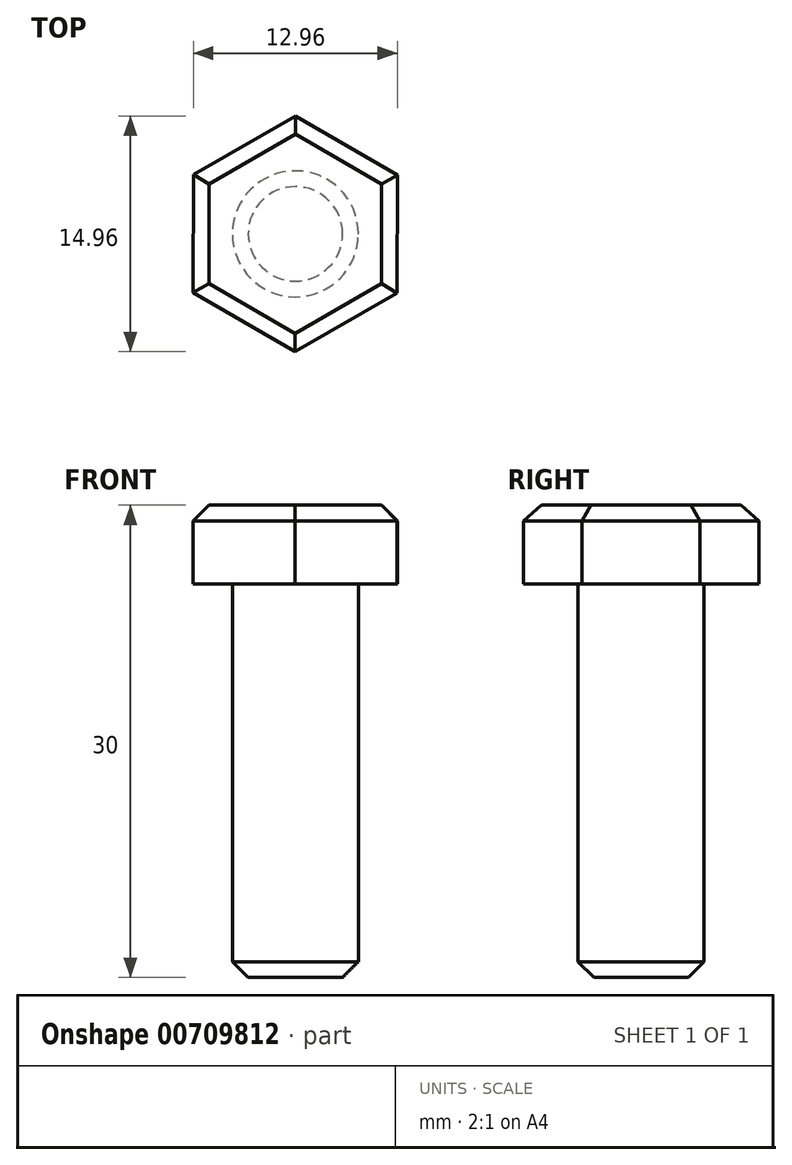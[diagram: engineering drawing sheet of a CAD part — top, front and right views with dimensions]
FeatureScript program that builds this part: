
annotation { "Feature Type Name" : "Feature", "Feature Type Description" : "" }
export const myFeature = defineFeature(function(context is Context, id is Id, definition is map)
    precondition{}
    {
        {
            var Q0;
            Q0=qCreatedBy(makeId("Top.planeOp"),FACE);
            var sketch = newSketch(context, id + "F0", { "sketchPlane" : qUnion([Q0])});
            skCircle(sketch, "E0.cCircle", {"center": v(0, 0) * mm, "radius": 6.48 * mm, "construction": true});
            skLineSegment(sketch, "E0.0", {"start": v(6.47, -3.75) * mm, "end": v(-0.01, -7.48) * mm});
            skLineSegment(sketch, "E0.1", {"start": v(-0.01, -7.48) * mm, "end": v(-6.48, -3.73) * mm});
            skLineSegment(sketch, "E0.2", {"start": v(-6.48, -3.73) * mm, "end": v(-6.47, 3.75) * mm});
            skLineSegment(sketch, "E0.3", {"start": v(-6.47, 3.75) * mm, "end": v(0.01, 7.48) * mm});
            skLineSegment(sketch, "E0.4", {"start": v(0.01, 7.48) * mm, "end": v(6.48, 3.73) * mm});
            skLineSegment(sketch, "E0.5", {"start": v(6.48, 3.73) * mm, "end": v(6.47, -3.75) * mm});
            skPoint(sketch, "E0.0.midPoint", {"position": v(3.23, -5.61) * mm});
            skSolve(sketch);
        }
        {
            var Q0;
            Q0 = qSketchRegion(id + "F0", true);
            extrude(context, id + "F1", {"entities" : qUnion([Q0]), "depth" : 5 * mm, "offsetDistance" : 25 * mm});
        }
        {
            var Q0;
            Q0=qCreatedBy(makeId("Top.planeOp"),FACE);
            var sketch = newSketch(context, id + "F2", { "sketchPlane" : qUnion([Q0])});
            skCircle(sketch, "E1", {"center": v(0, 0) * mm, "radius": 4 * mm});
            skSolve(sketch);
        }
        {
            var Q0;
            Q0 = qSketchRegion(id + "F2", true);
            extrude(context, id + "F3", {"entities" : qUnion([Q0]), "operationType" : NewBodyOperationType.ADD, "oppositeDirection" : true, "depth" : 25 * mm, "offsetDistance" : 25 * mm});
        }
        {
            var Q0;
            Q0=makeQuery(id+"F3.opExtrude","CAP_EDGE",EDGE,{"disambiguationData":[OSD([sQuery(id+"F2.wireOp",EDGE,"E1")])],"isStart":false});
            chamfer(context, id + "F4", {"entities" : qUnion([Q0]), "width" : 1 * mm, "tangentPropagation" : true});
        }
        {
            var Q0;
            Q0=makeQuery(id+"F1.opExtrude","CAP_EDGE",EDGE,{"disambiguationData":[OSD([sQuery(id+"F0.wireOp",EDGE,"E0.5")])],"isStart":false});
            var Q1;
            Q1=makeQuery(id+"F1.opExtrude","CAP_EDGE",EDGE,{"disambiguationData":[OSD([sQuery(id+"F0.wireOp",EDGE,"E0.0")])],"isStart":false});
            var Q2;
            Q2=makeQuery(id+"F1.opExtrude","CAP_EDGE",EDGE,{"disambiguationData":[OSD([sQuery(id+"F0.wireOp",EDGE,"E0.4")])],"isStart":false});
            var Q3;
            Q3=makeQuery(id+"F1.opExtrude","CAP_EDGE",EDGE,{"disambiguationData":[OSD([sQuery(id+"F0.wireOp",EDGE,"E0.2")])],"isStart":false});
            var Q4;
            Q4=makeQuery(id+"F1.opExtrude","CAP_EDGE",EDGE,{"disambiguationData":[OSD([sQuery(id+"F0.wireOp",EDGE,"E0.1")])],"isStart":false});
            var Q5;
            Q5=makeQuery(id+"F1.opExtrude","CAP_EDGE",EDGE,{"disambiguationData":[OSD([sQuery(id+"F0.wireOp",EDGE,"E0.3")])],"isStart":false});
            chamfer(context, id + "F5", {"entities" : qUnion([Q0, Q1, Q2, Q3, Q4, Q5]), "width" : 1 * mm, "tangentPropagation" : true});
        }
    });
